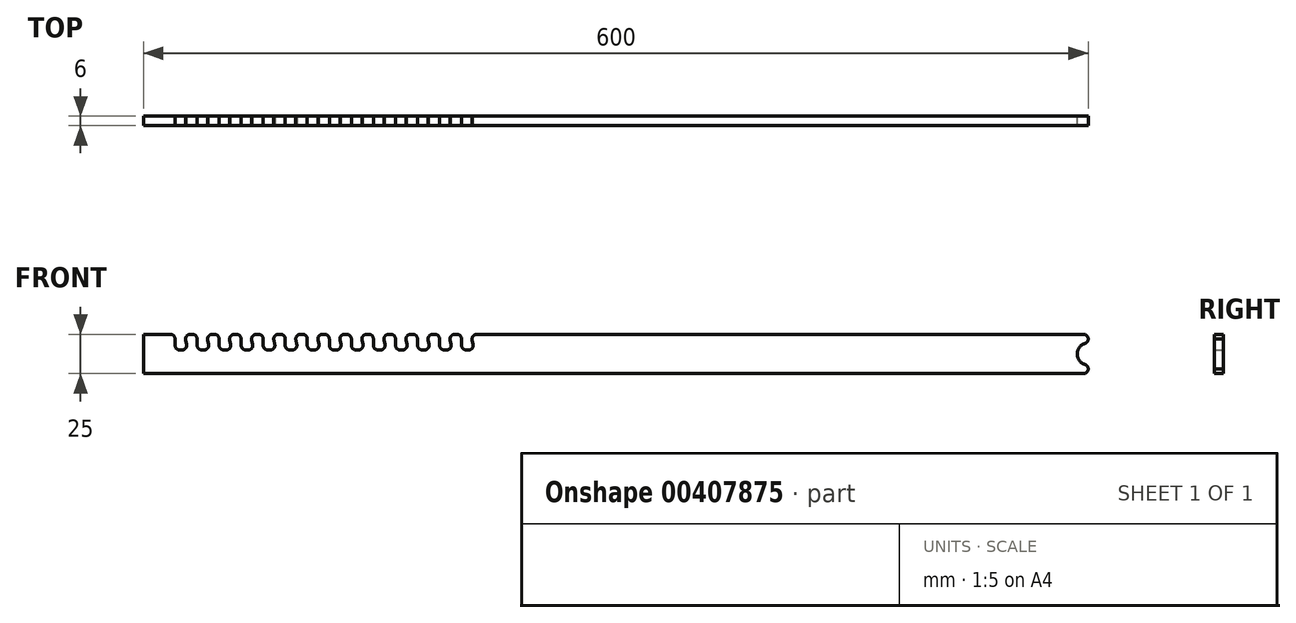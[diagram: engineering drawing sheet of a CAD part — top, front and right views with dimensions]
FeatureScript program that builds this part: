
annotation { "Feature Type Name" : "Feature", "Feature Type Description" : "" }
export const myFeature = defineFeature(function(context is Context, id is Id, definition is map)
    precondition{}
    {
        {
            var Q0;
            Q0=qCreatedBy(makeId("Front.planeOp"),FACE);
            var sketch = newSketch(context, id + "F0", { "sketchPlane" : qUnion([Q0])});
            skLineSegment(sketch, "E0.bottom", {"start": v(0, 0) * mm, "end": v(600, 0) * mm});
            skLineSegment(sketch, "E0.top", {"start": v(0, 25) * mm, "end": v(600, 25) * mm});
            skLineSegment(sketch, "E0.left", {"start": v(0, 0) * mm, "end": v(0, 25) * mm});
            skLineSegment(sketch, "E0.right", {"start": v(600, 0) * mm, "end": v(600, 25) * mm});
            skArc(sketch, "E1", {"start": v(600, 19.5) * mm, "mid": v(593, 12.5) * mm, "end": v(600, 5.5) * mm});
            skLineSegment(sketch, "E2.bottom", {"start": v(20, 25) * mm, "end": v(26, 25) * mm});
            skLineSegment(sketch, "E2.top", {"start": v(20, 15) * mm, "end": v(26, 15) * mm});
            skLineSegment(sketch, "E2.left", {"start": v(20, 25) * mm, "end": v(20, 15) * mm});
            skLineSegment(sketch, "E2.right", {"start": v(26, 25) * mm, "end": v(26, 15) * mm});
            skLineSegment(sketch, "E3.1.0.0", {"start": v(34, 25) * mm, "end": v(40, 25) * mm});
            skLineSegment(sketch, "E3.1.0.1", {"start": v(34, 25) * mm, "end": v(34, 15) * mm});
            skLineSegment(sketch, "E3.1.0.2", {"start": v(34, 15) * mm, "end": v(40, 15) * mm});
            skLineSegment(sketch, "E3.1.0.3", {"start": v(40, 25) * mm, "end": v(40, 15) * mm});
            skLineSegment(sketch, "E3.2.0.0", {"start": v(48, 25) * mm, "end": v(54, 25) * mm});
            skLineSegment(sketch, "E3.2.0.1", {"start": v(48, 25) * mm, "end": v(48, 15) * mm});
            skLineSegment(sketch, "E3.2.0.2", {"start": v(48, 15) * mm, "end": v(54, 15) * mm});
            skLineSegment(sketch, "E3.2.0.3", {"start": v(54, 25) * mm, "end": v(54, 15) * mm});
            skLineSegment(sketch, "E3.3.0.0", {"start": v(62, 25) * mm, "end": v(68, 25) * mm});
            skLineSegment(sketch, "E3.3.0.1", {"start": v(62, 25) * mm, "end": v(62, 15) * mm});
            skLineSegment(sketch, "E3.3.0.2", {"start": v(62, 15) * mm, "end": v(68, 15) * mm});
            skLineSegment(sketch, "E3.3.0.3", {"start": v(68, 25) * mm, "end": v(68, 15) * mm});
            skLineSegment(sketch, "E3.4.0.0", {"start": v(76, 25) * mm, "end": v(82, 25) * mm});
            skLineSegment(sketch, "E3.4.0.1", {"start": v(76, 25) * mm, "end": v(76, 15) * mm});
            skLineSegment(sketch, "E3.4.0.2", {"start": v(76, 15) * mm, "end": v(82, 15) * mm});
            skLineSegment(sketch, "E3.4.0.3", {"start": v(82, 25) * mm, "end": v(82, 15) * mm});
            skLineSegment(sketch, "E3.5.0.0", {"start": v(90, 25) * mm, "end": v(96, 25) * mm});
            skLineSegment(sketch, "E3.5.0.1", {"start": v(90, 25) * mm, "end": v(90, 15) * mm});
            skLineSegment(sketch, "E3.5.0.2", {"start": v(90, 15) * mm, "end": v(96, 15) * mm});
            skLineSegment(sketch, "E3.5.0.3", {"start": v(96, 25) * mm, "end": v(96, 15) * mm});
            skLineSegment(sketch, "E3.6.0.0", {"start": v(104, 25) * mm, "end": v(110, 25) * mm});
            skLineSegment(sketch, "E3.6.0.1", {"start": v(104, 25) * mm, "end": v(104, 15) * mm});
            skLineSegment(sketch, "E3.6.0.2", {"start": v(104, 15) * mm, "end": v(110, 15) * mm});
            skLineSegment(sketch, "E3.6.0.3", {"start": v(110, 25) * mm, "end": v(110, 15) * mm});
            skLineSegment(sketch, "E3.7.0.0", {"start": v(118, 25) * mm, "end": v(124, 25) * mm});
            skLineSegment(sketch, "E3.7.0.1", {"start": v(118, 25) * mm, "end": v(118, 15) * mm});
            skLineSegment(sketch, "E3.7.0.2", {"start": v(118, 15) * mm, "end": v(124, 15) * mm});
            skLineSegment(sketch, "E3.7.0.3", {"start": v(124, 25) * mm, "end": v(124, 15) * mm});
            skLineSegment(sketch, "E3.8.0.0", {"start": v(132, 25) * mm, "end": v(138, 25) * mm});
            skLineSegment(sketch, "E3.8.0.1", {"start": v(132, 25) * mm, "end": v(132, 15) * mm});
            skLineSegment(sketch, "E3.8.0.2", {"start": v(132, 15) * mm, "end": v(138, 15) * mm});
            skLineSegment(sketch, "E3.8.0.3", {"start": v(138, 25) * mm, "end": v(138, 15) * mm});
            skLineSegment(sketch, "E3.9.0.0", {"start": v(146, 25) * mm, "end": v(152, 25) * mm});
            skLineSegment(sketch, "E3.9.0.1", {"start": v(146, 25) * mm, "end": v(146, 15) * mm});
            skLineSegment(sketch, "E3.9.0.2", {"start": v(146, 15) * mm, "end": v(152, 15) * mm});
            skLineSegment(sketch, "E3.9.0.3", {"start": v(152, 25) * mm, "end": v(152, 15) * mm});
            skLineSegment(sketch, "E3.10.0.0", {"start": v(160, 25) * mm, "end": v(166, 25) * mm});
            skLineSegment(sketch, "E3.10.0.1", {"start": v(160, 25) * mm, "end": v(160, 15) * mm});
            skLineSegment(sketch, "E3.10.0.2", {"start": v(160, 15) * mm, "end": v(166, 15) * mm});
            skLineSegment(sketch, "E3.10.0.3", {"start": v(166, 25) * mm, "end": v(166, 15) * mm});
            skLineSegment(sketch, "E3.11.0.0", {"start": v(174, 25) * mm, "end": v(180, 25) * mm});
            skLineSegment(sketch, "E3.11.0.1", {"start": v(174, 25) * mm, "end": v(174, 15) * mm});
            skLineSegment(sketch, "E3.11.0.2", {"start": v(174, 15) * mm, "end": v(180, 15) * mm});
            skLineSegment(sketch, "E3.11.0.3", {"start": v(180, 25) * mm, "end": v(180, 15) * mm});
            skLineSegment(sketch, "E3.12.0.0", {"start": v(188, 25) * mm, "end": v(194, 25) * mm});
            skLineSegment(sketch, "E3.12.0.1", {"start": v(188, 25) * mm, "end": v(188, 15) * mm});
            skLineSegment(sketch, "E3.12.0.2", {"start": v(188, 15) * mm, "end": v(194, 15) * mm});
            skLineSegment(sketch, "E3.12.0.3", {"start": v(194, 25) * mm, "end": v(194, 15) * mm});
            skLineSegment(sketch, "E3.13.0.0", {"start": v(202, 25) * mm, "end": v(208, 25) * mm});
            skLineSegment(sketch, "E3.13.0.1", {"start": v(202, 25) * mm, "end": v(202, 15) * mm});
            skLineSegment(sketch, "E3.13.0.2", {"start": v(202, 15) * mm, "end": v(208, 15) * mm});
            skLineSegment(sketch, "E3.13.0.3", {"start": v(208, 25) * mm, "end": v(208, 15) * mm});
            skLineSegment(sketch, "E3.direction1", {"start": v(20, 25) * mm, "end": v(34, 25) * mm, "construction": true});
            skLineSegment(sketch, "E4", {"start": v(26, 25) * mm, "end": v(28.13, 15) * mm});
            skLineSegment(sketch, "E5", {"start": v(28.13, 15) * mm, "end": v(26, 15) * mm});
            skLineSegment(sketch, "E6.1.0.0", {"start": v(40, 25) * mm, "end": v(42.13, 15) * mm});
            skLineSegment(sketch, "E6.1.0.1", {"start": v(42.13, 15) * mm, "end": v(40, 15) * mm});
            skLineSegment(sketch, "E6.2.0.0", {"start": v(54, 25) * mm, "end": v(56.13, 15) * mm});
            skLineSegment(sketch, "E6.2.0.1", {"start": v(56.13, 15) * mm, "end": v(54, 15) * mm});
            skLineSegment(sketch, "E6.3.0.0", {"start": v(68, 25) * mm, "end": v(70.13, 15) * mm});
            skLineSegment(sketch, "E6.3.0.1", {"start": v(70.13, 15) * mm, "end": v(68, 15) * mm});
            skLineSegment(sketch, "E6.4.0.0", {"start": v(82, 25) * mm, "end": v(84.13, 15) * mm});
            skLineSegment(sketch, "E6.4.0.1", {"start": v(84.13, 15) * mm, "end": v(82, 15) * mm});
            skLineSegment(sketch, "E6.5.0.0", {"start": v(96, 25) * mm, "end": v(98.13, 15) * mm});
            skLineSegment(sketch, "E6.5.0.1", {"start": v(98.13, 15) * mm, "end": v(96, 15) * mm});
            skLineSegment(sketch, "E6.6.0.0", {"start": v(110, 25) * mm, "end": v(112.13, 15) * mm});
            skLineSegment(sketch, "E6.6.0.1", {"start": v(112.13, 15) * mm, "end": v(110, 15) * mm});
            skLineSegment(sketch, "E6.7.0.0", {"start": v(124, 25) * mm, "end": v(126.13, 15) * mm});
            skLineSegment(sketch, "E6.7.0.1", {"start": v(126.13, 15) * mm, "end": v(124, 15) * mm});
            skLineSegment(sketch, "E6.8.0.0", {"start": v(138, 25) * mm, "end": v(140.13, 15) * mm});
            skLineSegment(sketch, "E6.8.0.1", {"start": v(140.13, 15) * mm, "end": v(138, 15) * mm});
            skLineSegment(sketch, "E6.9.0.0", {"start": v(152, 25) * mm, "end": v(154.13, 15) * mm});
            skLineSegment(sketch, "E6.9.0.1", {"start": v(154.13, 15) * mm, "end": v(152, 15) * mm});
            skLineSegment(sketch, "E6.10.0.0", {"start": v(166, 25) * mm, "end": v(168.13, 15) * mm});
            skLineSegment(sketch, "E6.10.0.1", {"start": v(168.13, 15) * mm, "end": v(166, 15) * mm});
            skLineSegment(sketch, "E6.11.0.0", {"start": v(180, 25) * mm, "end": v(182.13, 15) * mm});
            skLineSegment(sketch, "E6.11.0.1", {"start": v(182.13, 15) * mm, "end": v(180, 15) * mm});
            skLineSegment(sketch, "E6.12.0.0", {"start": v(194, 25) * mm, "end": v(196.13, 15) * mm});
            skLineSegment(sketch, "E6.12.0.1", {"start": v(196.13, 15) * mm, "end": v(194, 15) * mm});
            skLineSegment(sketch, "E6.13.0.0", {"start": v(208, 25) * mm, "end": v(210.13, 15) * mm});
            skLineSegment(sketch, "E6.13.0.1", {"start": v(210.13, 15) * mm, "end": v(208, 15) * mm});
            skLineSegment(sketch, "E6.direction1", {"start": v(28.13, 15) * mm, "end": v(42.13, 15) * mm, "construction": true});
            skSolve(sketch);
        }
        {
            var Q0;
            {var subQ24=sQuery(id+"F0.wireOp",EDGE,"E0.bottom");Q0=makeQuery(id+"F0.imprint","IMPRINT",FACE,{"disambiguationData":[TD([[makeQuery(id+"F0.imprint","IMPRINT",EDGE,{"derivedFrom":subQ24}),1.0]])]});}
            extrude(context, id + "F1", {"entities" : qUnion([Q0]), "depth" : 6 * mm});
        }
        {
            var Q0;
            Q0=makeQuery(id+"F1.opExtrude","SWEPT_EDGE",EDGE,{"disambiguationData":[OSD([sQuery(id+"F0.wireOp",EDGE,"E2.top"),sQuery(id+"F0.wireOp",EDGE,"E2.left")])]});
            var Q1;
            Q1=makeQuery(id+"F1.opExtrude","SWEPT_EDGE",EDGE,{"disambiguationData":[OSD([sQuery(id+"F0.wireOp",EDGE,"E2.top"),sQuery(id+"F0.wireOp",EDGE,"E2.right")])]});
            var Q2;
            Q2=makeQuery(id+"F1.opExtrude","SWEPT_EDGE",EDGE,{"disambiguationData":[OSD([sQuery(id+"F0.wireOp",EDGE,"E0.top"),sQuery(id+"F0.wireOp",EDGE,"E2.bottom"),sQuery(id+"F0.wireOp",EDGE,"E2.right")])]});
            var Q3;
            Q3=makeQuery(id+"F1.opExtrude","SWEPT_EDGE",EDGE,{"disambiguationData":[OSD([sQuery(id+"F0.wireOp",EDGE,"E0.top"),sQuery(id+"F0.wireOp",EDGE,"E2.bottom"),sQuery(id+"F0.wireOp",EDGE,"E2.left")])]});
            var Q4;
            Q4=makeQuery(id+"F1.opExtrude","SWEPT_EDGE",EDGE,{"disambiguationData":[OSD([sQuery(id+"F0.wireOp",EDGE,"E0.top"),sQuery(id+"F0.wireOp",EDGE,"E3.1.0.0"),sQuery(id+"F0.wireOp",EDGE,"E3.1.0.1")])]});
            var Q5;
            Q5=makeQuery(id+"F1.opExtrude","SWEPT_EDGE",EDGE,{"disambiguationData":[OSD([sQuery(id+"F0.wireOp",EDGE,"E3.1.0.2"),sQuery(id+"F0.wireOp",EDGE,"E3.1.0.3")])]});
            var Q6;
            Q6=makeQuery(id+"F1.opExtrude","SWEPT_EDGE",EDGE,{"disambiguationData":[OSD([sQuery(id+"F0.wireOp",EDGE,"E0.top"),sQuery(id+"F0.wireOp",EDGE,"E3.1.0.0"),sQuery(id+"F0.wireOp",EDGE,"E3.1.0.3")])]});
            var Q7;
            Q7=makeQuery(id+"F1.opExtrude","SWEPT_EDGE",EDGE,{"disambiguationData":[OSD([sQuery(id+"F0.wireOp",EDGE,"E0.top"),sQuery(id+"F0.wireOp",EDGE,"E3.2.0.0"),sQuery(id+"F0.wireOp",EDGE,"E3.2.0.1")])]});
            var Q8;
            Q8=makeQuery(id+"F1.opExtrude","SWEPT_EDGE",EDGE,{"disambiguationData":[OSD([sQuery(id+"F0.wireOp",EDGE,"E0.top"),sQuery(id+"F0.wireOp",EDGE,"E3.2.0.0"),sQuery(id+"F0.wireOp",EDGE,"E3.2.0.3")])]});
            var Q9;
            Q9=makeQuery(id+"F1.opExtrude","SWEPT_EDGE",EDGE,{"disambiguationData":[OSD([sQuery(id+"F0.wireOp",EDGE,"E3.2.0.2"),sQuery(id+"F0.wireOp",EDGE,"E3.2.0.3")])]});
            var Q10;
            Q10=makeQuery(id+"F1.opExtrude","SWEPT_EDGE",EDGE,{"disambiguationData":[OSD([sQuery(id+"F0.wireOp",EDGE,"E0.top"),sQuery(id+"F0.wireOp",EDGE,"E3.3.0.0"),sQuery(id+"F0.wireOp",EDGE,"E3.3.0.1")])]});
            var Q11;
            Q11=makeQuery(id+"F1.opExtrude","SWEPT_EDGE",EDGE,{"disambiguationData":[OSD([sQuery(id+"F0.wireOp",EDGE,"E3.3.0.2"),sQuery(id+"F0.wireOp",EDGE,"E3.3.0.3")])]});
            var Q12;
            Q12=makeQuery(id+"F1.opExtrude","SWEPT_EDGE",EDGE,{"disambiguationData":[OSD([sQuery(id+"F0.wireOp",EDGE,"E0.top"),sQuery(id+"F0.wireOp",EDGE,"E3.3.0.0"),sQuery(id+"F0.wireOp",EDGE,"E3.3.0.3")])]});
            var Q13;
            Q13=makeQuery(id+"F1.opExtrude","SWEPT_EDGE",EDGE,{"disambiguationData":[OSD([sQuery(id+"F0.wireOp",EDGE,"E0.top"),sQuery(id+"F0.wireOp",EDGE,"E3.4.0.0"),sQuery(id+"F0.wireOp",EDGE,"E3.4.0.1")])]});
            var Q14;
            Q14=makeQuery(id+"F1.opExtrude","SWEPT_EDGE",EDGE,{"disambiguationData":[OSD([sQuery(id+"F0.wireOp",EDGE,"E3.4.0.2"),sQuery(id+"F0.wireOp",EDGE,"E3.4.0.3")])]});
            var Q15;
            Q15=makeQuery(id+"F1.opExtrude","SWEPT_EDGE",EDGE,{"disambiguationData":[OSD([sQuery(id+"F0.wireOp",EDGE,"E0.top"),sQuery(id+"F0.wireOp",EDGE,"E3.4.0.0"),sQuery(id+"F0.wireOp",EDGE,"E3.4.0.3")])]});
            var Q16;
            Q16=makeQuery(id+"F1.opExtrude","SWEPT_EDGE",EDGE,{"disambiguationData":[OSD([sQuery(id+"F0.wireOp",EDGE,"E0.top"),sQuery(id+"F0.wireOp",EDGE,"E3.5.0.0"),sQuery(id+"F0.wireOp",EDGE,"E3.5.0.1")])]});
            var Q17;
            Q17=makeQuery(id+"F1.opExtrude","SWEPT_EDGE",EDGE,{"disambiguationData":[OSD([sQuery(id+"F0.wireOp",EDGE,"E3.5.0.2"),sQuery(id+"F0.wireOp",EDGE,"E3.5.0.3")])]});
            var Q18;
            Q18=makeQuery(id+"F1.opExtrude","SWEPT_EDGE",EDGE,{"disambiguationData":[OSD([sQuery(id+"F0.wireOp",EDGE,"E0.top"),sQuery(id+"F0.wireOp",EDGE,"E3.5.0.0"),sQuery(id+"F0.wireOp",EDGE,"E3.5.0.3")])]});
            var Q19;
            Q19=makeQuery(id+"F1.opExtrude","SWEPT_EDGE",EDGE,{"disambiguationData":[OSD([sQuery(id+"F0.wireOp",EDGE,"E0.top"),sQuery(id+"F0.wireOp",EDGE,"E3.6.0.0"),sQuery(id+"F0.wireOp",EDGE,"E3.6.0.1")])]});
            var Q20;
            Q20=makeQuery(id+"F1.opExtrude","SWEPT_EDGE",EDGE,{"disambiguationData":[OSD([sQuery(id+"F0.wireOp",EDGE,"E3.6.0.2"),sQuery(id+"F0.wireOp",EDGE,"E3.6.0.3")])]});
            var Q21;
            Q21=makeQuery(id+"F1.opExtrude","SWEPT_EDGE",EDGE,{"disambiguationData":[OSD([sQuery(id+"F0.wireOp",EDGE,"E0.top"),sQuery(id+"F0.wireOp",EDGE,"E3.6.0.0"),sQuery(id+"F0.wireOp",EDGE,"E3.6.0.3")])]});
            var Q22;
            Q22=makeQuery(id+"F1.opExtrude","SWEPT_EDGE",EDGE,{"disambiguationData":[OSD([sQuery(id+"F0.wireOp",EDGE,"E0.top"),sQuery(id+"F0.wireOp",EDGE,"E3.7.0.0"),sQuery(id+"F0.wireOp",EDGE,"E3.7.0.1")])]});
            var Q23;
            Q23=makeQuery(id+"F1.opExtrude","SWEPT_EDGE",EDGE,{"disambiguationData":[OSD([sQuery(id+"F0.wireOp",EDGE,"E3.7.0.2"),sQuery(id+"F0.wireOp",EDGE,"E3.7.0.3")])]});
            var Q24;
            Q24=makeQuery(id+"F1.opExtrude","SWEPT_EDGE",EDGE,{"disambiguationData":[OSD([sQuery(id+"F0.wireOp",EDGE,"E0.top"),sQuery(id+"F0.wireOp",EDGE,"E3.7.0.0"),sQuery(id+"F0.wireOp",EDGE,"E3.7.0.3")])]});
            var Q25;
            Q25=makeQuery(id+"F1.opExtrude","SWEPT_EDGE",EDGE,{"disambiguationData":[OSD([sQuery(id+"F0.wireOp",EDGE,"E0.top"),sQuery(id+"F0.wireOp",EDGE,"E3.8.0.0"),sQuery(id+"F0.wireOp",EDGE,"E3.8.0.1")])]});
            var Q26;
            Q26=makeQuery(id+"F1.opExtrude","SWEPT_EDGE",EDGE,{"disambiguationData":[OSD([sQuery(id+"F0.wireOp",EDGE,"E3.8.0.2"),sQuery(id+"F0.wireOp",EDGE,"E3.8.0.3")])]});
            var Q27;
            Q27=makeQuery(id+"F1.opExtrude","SWEPT_EDGE",EDGE,{"disambiguationData":[OSD([sQuery(id+"F0.wireOp",EDGE,"E0.top"),sQuery(id+"F0.wireOp",EDGE,"E3.8.0.0"),sQuery(id+"F0.wireOp",EDGE,"E3.8.0.3")])]});
            var Q28;
            Q28=makeQuery(id+"F1.opExtrude","SWEPT_EDGE",EDGE,{"disambiguationData":[OSD([sQuery(id+"F0.wireOp",EDGE,"E0.top"),sQuery(id+"F0.wireOp",EDGE,"E3.9.0.0"),sQuery(id+"F0.wireOp",EDGE,"E3.9.0.1")])]});
            var Q29;
            Q29=makeQuery(id+"F1.opExtrude","SWEPT_EDGE",EDGE,{"disambiguationData":[OSD([sQuery(id+"F0.wireOp",EDGE,"E3.9.0.2"),sQuery(id+"F0.wireOp",EDGE,"E3.9.0.3")])]});
            var Q30;
            Q30=makeQuery(id+"F1.opExtrude","SWEPT_EDGE",EDGE,{"disambiguationData":[OSD([sQuery(id+"F0.wireOp",EDGE,"E0.top"),sQuery(id+"F0.wireOp",EDGE,"E3.9.0.0"),sQuery(id+"F0.wireOp",EDGE,"E3.9.0.3")])]});
            var Q31;
            Q31=makeQuery(id+"F1.opExtrude","SWEPT_EDGE",EDGE,{"disambiguationData":[OSD([sQuery(id+"F0.wireOp",EDGE,"E0.top"),sQuery(id+"F0.wireOp",EDGE,"E3.10.0.0"),sQuery(id+"F0.wireOp",EDGE,"E3.10.0.1")])]});
            var Q32;
            Q32=makeQuery(id+"F1.opExtrude","SWEPT_EDGE",EDGE,{"disambiguationData":[OSD([sQuery(id+"F0.wireOp",EDGE,"E3.10.0.2"),sQuery(id+"F0.wireOp",EDGE,"E3.10.0.3")])]});
            var Q33;
            Q33=makeQuery(id+"F1.opExtrude","SWEPT_EDGE",EDGE,{"disambiguationData":[OSD([sQuery(id+"F0.wireOp",EDGE,"E0.top"),sQuery(id+"F0.wireOp",EDGE,"E3.10.0.0"),sQuery(id+"F0.wireOp",EDGE,"E3.10.0.3")])]});
            var Q34;
            Q34=makeQuery(id+"F1.opExtrude","SWEPT_EDGE",EDGE,{"disambiguationData":[OSD([sQuery(id+"F0.wireOp",EDGE,"E0.top"),sQuery(id+"F0.wireOp",EDGE,"E3.11.0.0"),sQuery(id+"F0.wireOp",EDGE,"E3.11.0.1")])]});
            var Q35;
            Q35=makeQuery(id+"F1.opExtrude","SWEPT_EDGE",EDGE,{"disambiguationData":[OSD([sQuery(id+"F0.wireOp",EDGE,"E3.11.0.2"),sQuery(id+"F0.wireOp",EDGE,"E3.11.0.3")])]});
            var Q36;
            Q36=makeQuery(id+"F1.opExtrude","SWEPT_EDGE",EDGE,{"disambiguationData":[OSD([sQuery(id+"F0.wireOp",EDGE,"E0.top"),sQuery(id+"F0.wireOp",EDGE,"E3.11.0.0"),sQuery(id+"F0.wireOp",EDGE,"E3.11.0.3")])]});
            var Q37;
            Q37=makeQuery(id+"F1.opExtrude","SWEPT_EDGE",EDGE,{"disambiguationData":[OSD([sQuery(id+"F0.wireOp",EDGE,"E0.top"),sQuery(id+"F0.wireOp",EDGE,"E3.12.0.0"),sQuery(id+"F0.wireOp",EDGE,"E3.12.0.1")])]});
            var Q38;
            Q38=makeQuery(id+"F1.opExtrude","SWEPT_EDGE",EDGE,{"disambiguationData":[OSD([sQuery(id+"F0.wireOp",EDGE,"E3.12.0.2"),sQuery(id+"F0.wireOp",EDGE,"E3.12.0.3")])]});
            var Q39;
            Q39=makeQuery(id+"F1.opExtrude","SWEPT_EDGE",EDGE,{"disambiguationData":[OSD([sQuery(id+"F0.wireOp",EDGE,"E0.top"),sQuery(id+"F0.wireOp",EDGE,"E3.12.0.0"),sQuery(id+"F0.wireOp",EDGE,"E3.12.0.3")])]});
            var Q40;
            Q40=makeQuery(id+"F1.opExtrude","SWEPT_EDGE",EDGE,{"disambiguationData":[OSD([sQuery(id+"F0.wireOp",EDGE,"E3.13.0.2"),sQuery(id+"F0.wireOp",EDGE,"E3.13.0.3")])]});
            var Q41;
            Q41=makeQuery(id+"F1.opExtrude","SWEPT_EDGE",EDGE,{"disambiguationData":[OSD([sQuery(id+"F0.wireOp",EDGE,"E0.top"),sQuery(id+"F0.wireOp",EDGE,"E3.13.0.0"),sQuery(id+"F0.wireOp",EDGE,"E3.13.0.3")])]});
            var Q42;
            Q42=makeQuery(id+"F1.opExtrude","SWEPT_EDGE",EDGE,{"disambiguationData":[OSD([sQuery(id+"F0.wireOp",EDGE,"E0.top"),sQuery(id+"F0.wireOp",EDGE,"E3.13.0.0"),sQuery(id+"F0.wireOp",EDGE,"E3.13.0.1")])]});
            var Q43;
            Q43=makeQuery(id+"F1.opExtrude","SWEPT_EDGE",EDGE,{"disambiguationData":[OSD([sQuery(id+"F0.wireOp",EDGE,"E3.13.0.1"),sQuery(id+"F0.wireOp",EDGE,"E3.13.0.2")])]});
            var Q44;
            Q44=makeQuery(id+"F1.opExtrude","SWEPT_EDGE",EDGE,{"disambiguationData":[OSD([sQuery(id+"F0.wireOp",EDGE,"E3.12.0.1"),sQuery(id+"F0.wireOp",EDGE,"E3.12.0.2")])]});
            var Q45;
            Q45=makeQuery(id+"F1.opExtrude","SWEPT_EDGE",EDGE,{"disambiguationData":[OSD([sQuery(id+"F0.wireOp",EDGE,"E3.11.0.1"),sQuery(id+"F0.wireOp",EDGE,"E3.11.0.2")])]});
            var Q46;
            Q46=makeQuery(id+"F1.opExtrude","SWEPT_EDGE",EDGE,{"disambiguationData":[OSD([sQuery(id+"F0.wireOp",EDGE,"E3.10.0.1"),sQuery(id+"F0.wireOp",EDGE,"E3.10.0.2")])]});
            var Q47;
            Q47=makeQuery(id+"F1.opExtrude","SWEPT_EDGE",EDGE,{"disambiguationData":[OSD([sQuery(id+"F0.wireOp",EDGE,"E3.8.0.1"),sQuery(id+"F0.wireOp",EDGE,"E3.8.0.2")])]});
            var Q48;
            Q48=makeQuery(id+"F1.opExtrude","SWEPT_EDGE",EDGE,{"disambiguationData":[OSD([sQuery(id+"F0.wireOp",EDGE,"E3.9.0.1"),sQuery(id+"F0.wireOp",EDGE,"E3.9.0.2")])]});
            var Q49;
            Q49=makeQuery(id+"F1.opExtrude","SWEPT_EDGE",EDGE,{"disambiguationData":[OSD([sQuery(id+"F0.wireOp",EDGE,"E3.7.0.1"),sQuery(id+"F0.wireOp",EDGE,"E3.7.0.2")])]});
            var Q50;
            Q50=makeQuery(id+"F1.opExtrude","SWEPT_EDGE",EDGE,{"disambiguationData":[OSD([sQuery(id+"F0.wireOp",EDGE,"E3.6.0.1"),sQuery(id+"F0.wireOp",EDGE,"E3.6.0.2")])]});
            var Q51;
            Q51=makeQuery(id+"F1.opExtrude","SWEPT_EDGE",EDGE,{"disambiguationData":[OSD([sQuery(id+"F0.wireOp",EDGE,"E3.5.0.1"),sQuery(id+"F0.wireOp",EDGE,"E3.5.0.2")])]});
            var Q52;
            Q52=makeQuery(id+"F1.opExtrude","SWEPT_EDGE",EDGE,{"disambiguationData":[OSD([sQuery(id+"F0.wireOp",EDGE,"E3.4.0.1"),sQuery(id+"F0.wireOp",EDGE,"E3.4.0.2")])]});
            var Q53;
            Q53=makeQuery(id+"F1.opExtrude","SWEPT_EDGE",EDGE,{"disambiguationData":[OSD([sQuery(id+"F0.wireOp",EDGE,"E3.3.0.1"),sQuery(id+"F0.wireOp",EDGE,"E3.3.0.2")])]});
            var Q54;
            Q54=makeQuery(id+"F1.opExtrude","SWEPT_EDGE",EDGE,{"disambiguationData":[OSD([sQuery(id+"F0.wireOp",EDGE,"E3.2.0.1"),sQuery(id+"F0.wireOp",EDGE,"E3.2.0.2")])]});
            var Q55;
            Q55=makeQuery(id+"F1.opExtrude","SWEPT_EDGE",EDGE,{"disambiguationData":[OSD([sQuery(id+"F0.wireOp",EDGE,"E3.1.0.1"),sQuery(id+"F0.wireOp",EDGE,"E3.1.0.2")])]});
            var Q56;
            Q56=makeQuery(id+"F1.opExtrude","SWEPT_EDGE",EDGE,{"disambiguationData":[OSD([sQuery(id+"F0.wireOp",EDGE,"E0.top"),sQuery(id+"F0.wireOp",EDGE,"E0.right")])]});
            var Q57;
            {var subQ0=sQuery(id+"F0.wireOp",EDGE,"E1");var subQ1=sQuery(id+"F0.wireOp",EDGE,"E0.right");Q57=makeQuery(id+"F1.opExtrude","SWEPT_EDGE",EDGE,{"disambiguationData":[OSD([subQ1,subQ0]),TDD([makeQuery(id+"F0.imprint","INTERSECT",VERTEX,{"disambiguationData":[OD(0.0)],"derivedFrom":[subQ1,subQ0]})])]});}
            var Q58;
            {var subQ0=sQuery(id+"F0.wireOp",EDGE,"E1");var subQ1=sQuery(id+"F0.wireOp",EDGE,"E0.right");Q58=makeQuery(id+"F1.opExtrude","SWEPT_EDGE",EDGE,{"disambiguationData":[OSD([subQ1,subQ0]),TDD([makeQuery(id+"F0.imprint","INTERSECT",VERTEX,{"disambiguationData":[OD(1.0)],"derivedFrom":[subQ1,subQ0]})])]});}
            var Q59;
            Q59=makeQuery(id+"F1.opExtrude","SWEPT_EDGE",EDGE,{"disambiguationData":[OSD([sQuery(id+"F0.wireOp",EDGE,"E0.bottom"),sQuery(id+"F0.wireOp",EDGE,"E0.right")])]});
            var Q60;
            Q60=makeQuery(id+"F1.opExtrude","SWEPT_EDGE",EDGE,{"disambiguationData":[OSD([sQuery(id+"F0.wireOp",EDGE,"E4"),sQuery(id+"F0.wireOp",EDGE,"E5")])]});
            var Q61;
            Q61=makeQuery(id+"F1.opExtrude","SWEPT_EDGE",EDGE,{"disambiguationData":[OSD([sQuery(id+"F0.wireOp",EDGE,"E6.1.0.0"),sQuery(id+"F0.wireOp",EDGE,"E6.1.0.1")])]});
            var Q62;
            Q62=makeQuery(id+"F1.opExtrude","SWEPT_EDGE",EDGE,{"disambiguationData":[OSD([sQuery(id+"F0.wireOp",EDGE,"E6.2.0.0"),sQuery(id+"F0.wireOp",EDGE,"E6.2.0.1")])]});
            var Q63;
            Q63=makeQuery(id+"F1.opExtrude","SWEPT_EDGE",EDGE,{"disambiguationData":[OSD([sQuery(id+"F0.wireOp",EDGE,"E6.3.0.0"),sQuery(id+"F0.wireOp",EDGE,"E6.3.0.1")])]});
            var Q64;
            Q64=makeQuery(id+"F1.opExtrude","SWEPT_EDGE",EDGE,{"disambiguationData":[OSD([sQuery(id+"F0.wireOp",EDGE,"E6.4.0.0"),sQuery(id+"F0.wireOp",EDGE,"E6.4.0.1")])]});
            var Q65;
            Q65=makeQuery(id+"F1.opExtrude","SWEPT_EDGE",EDGE,{"disambiguationData":[OSD([sQuery(id+"F0.wireOp",EDGE,"E6.5.0.0"),sQuery(id+"F0.wireOp",EDGE,"E6.5.0.1")])]});
            var Q66;
            Q66=makeQuery(id+"F1.opExtrude","SWEPT_EDGE",EDGE,{"disambiguationData":[OSD([sQuery(id+"F0.wireOp",EDGE,"E6.6.0.0"),sQuery(id+"F0.wireOp",EDGE,"E6.6.0.1")])]});
            var Q67;
            Q67=makeQuery(id+"F1.opExtrude","SWEPT_EDGE",EDGE,{"disambiguationData":[OSD([sQuery(id+"F0.wireOp",EDGE,"E6.7.0.0"),sQuery(id+"F0.wireOp",EDGE,"E6.7.0.1")])]});
            var Q68;
            Q68=makeQuery(id+"F1.opExtrude","SWEPT_EDGE",EDGE,{"disambiguationData":[OSD([sQuery(id+"F0.wireOp",EDGE,"E6.8.0.0"),sQuery(id+"F0.wireOp",EDGE,"E6.8.0.1")])]});
            var Q69;
            Q69=makeQuery(id+"F1.opExtrude","SWEPT_EDGE",EDGE,{"disambiguationData":[OSD([sQuery(id+"F0.wireOp",EDGE,"E6.9.0.0"),sQuery(id+"F0.wireOp",EDGE,"E6.9.0.1")])]});
            var Q70;
            Q70=makeQuery(id+"F1.opExtrude","SWEPT_EDGE",EDGE,{"disambiguationData":[OSD([sQuery(id+"F0.wireOp",EDGE,"E6.10.0.0"),sQuery(id+"F0.wireOp",EDGE,"E6.10.0.1")])]});
            var Q71;
            Q71=makeQuery(id+"F1.opExtrude","SWEPT_EDGE",EDGE,{"disambiguationData":[OSD([sQuery(id+"F0.wireOp",EDGE,"E6.11.0.0"),sQuery(id+"F0.wireOp",EDGE,"E6.11.0.1")])]});
            var Q72;
            Q72=makeQuery(id+"F1.opExtrude","SWEPT_EDGE",EDGE,{"disambiguationData":[OSD([sQuery(id+"F0.wireOp",EDGE,"E6.12.0.0"),sQuery(id+"F0.wireOp",EDGE,"E6.12.0.1")])]});
            var Q73;
            Q73=makeQuery(id+"F1.opExtrude","SWEPT_EDGE",EDGE,{"disambiguationData":[OSD([sQuery(id+"F0.wireOp",EDGE,"E6.13.0.0"),sQuery(id+"F0.wireOp",EDGE,"E6.13.0.1")])]});
            fillet(context, id + "F2", {"entities" : qUnion([Q0, Q1, Q2, Q3, Q4, Q5, Q6, Q7, Q8, Q9, Q10, Q11, Q12, Q13, Q14, Q15, Q16, Q17, Q18, Q19, Q20, Q21, Q22, Q23, Q24, Q25, Q26, Q27, Q28, Q29, Q30, Q31, Q32, Q33, Q34, Q35, Q36, Q37, Q38, Q39, Q40, Q41, Q42, Q43, Q44, Q45, Q46, Q47, Q48, Q49, Q50, Q51, Q52, Q53, Q54, Q55, Q56, Q57, Q58, Q59, Q60, Q61, Q62, Q63, Q64, Q65, Q66, Q67, Q68, Q69, Q70, Q71, Q72, Q73]), "radius" : 3 * mm, "tangentPropagation" : true, "allowEdgeOverflow" : false});
        }
    });
